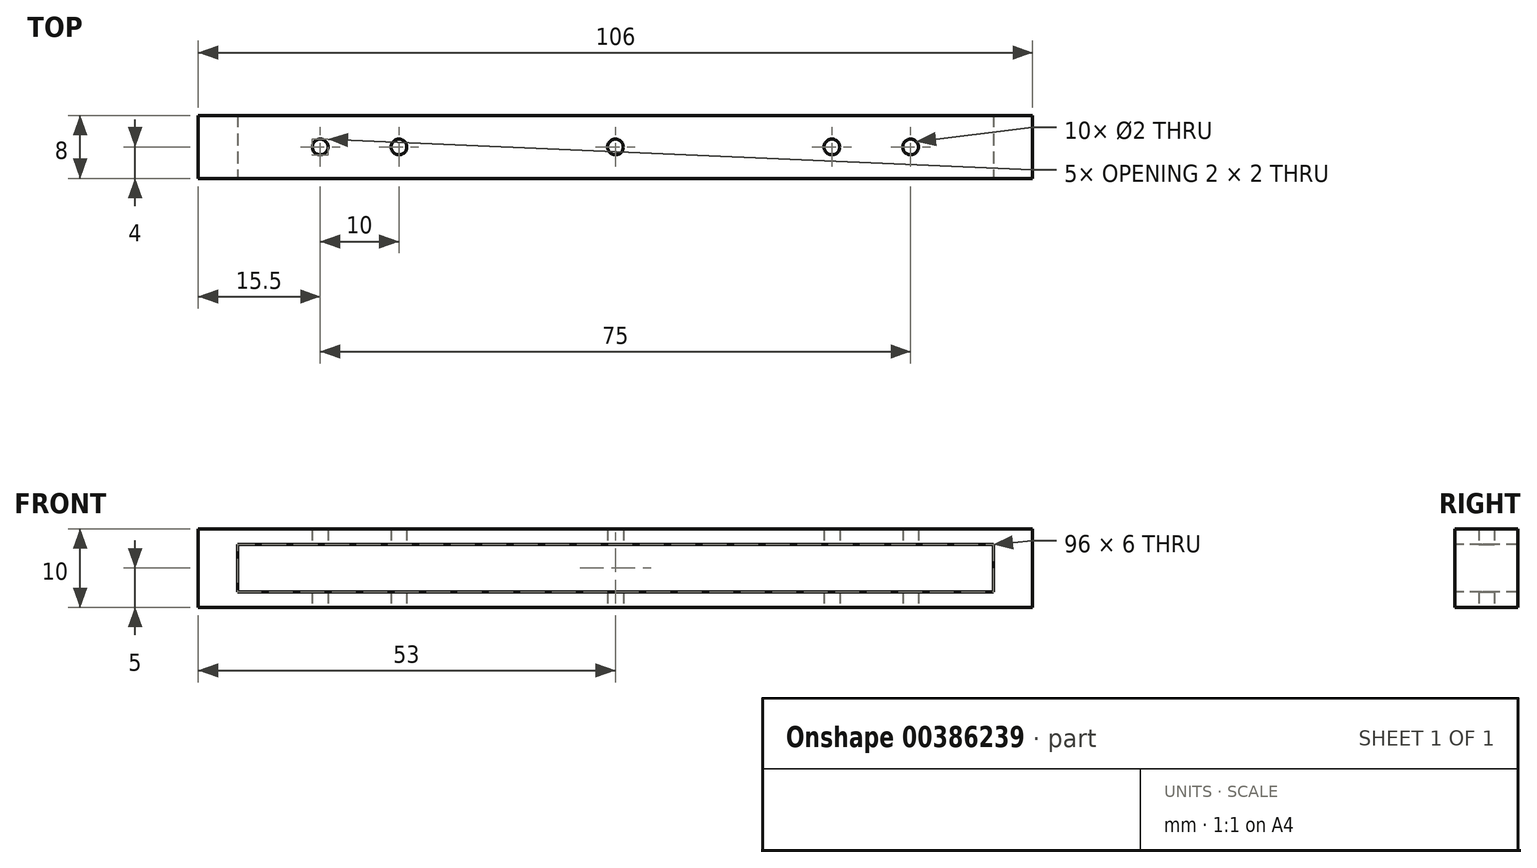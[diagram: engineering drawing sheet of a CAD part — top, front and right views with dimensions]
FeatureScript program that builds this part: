
annotation { "Feature Type Name" : "Feature", "Feature Type Description" : "" }
export const myFeature = defineFeature(function(context is Context, id is Id, definition is map)
    precondition{}
    {
        {
            assignVariable(context, id + "F0", {"name" : "height", "anyValue" : 10});
        }
        {
            var Q0;
            Q0=qCreatedBy(makeId("Top.planeOp"),FACE);
            var sketch = newSketch(context, id + "F1", { "sketchPlane" : qUnion([Q0])});
            skCircle(sketch, "E0", {"center": v(0, 0) * mm, "radius": 1 * mm});
            skCircle(sketch, "E1", {"center": v(37.5, 0) * mm, "radius": 1 * mm});
            skCircle(sketch, "E2", {"center": v(-37.5, 0) * mm, "radius": 1 * mm});
            skCircle(sketch, "E3", {"center": v(-27.5, 0) * mm, "radius": 1 * mm});
            skCircle(sketch, "E4", {"center": v(27.5, 0) * mm, "radius": 1 * mm});
            skLineSegment(sketch, "E5.bottom", {"start": v(-53, 4) * mm, "end": v(53, 4) * mm});
            skLineSegment(sketch, "E5.top", {"start": v(-53, -4) * mm, "end": v(53, -4) * mm});
            skLineSegment(sketch, "E5.left", {"start": v(-53, 4) * mm, "end": v(-53, -4) * mm});
            skLineSegment(sketch, "E5.right", {"start": v(53, 4) * mm, "end": v(53, -4) * mm});
            skSolve(sketch);
        }
        {
            var Q0;
            Q0=makeQuery(id+"F1.imprint","IMPRINT",FACE,{"disambiguationData":[TD([[makeQuery(id+"F1.imprint","IMPRINT",EDGE,{"derivedFrom":sQuery(id+"F1.wireOp",EDGE,"E0")}),-1.0]])]});
            var Q1;
            {var subQ0=sQuery(id+"F1.wireOp",EDGE,"E5.left");Q1=makeQuery(id+"F1.imprint","IMPRINT",FACE,{"disambiguationData":[TD([[makeQuery(id+"F1.imprint","IMPRINT",EDGE,{"derivedFrom":subQ0}),1.0]])]});}
            var Q2;
            {var subQ0=sQuery(id+"F1.wireOp",EDGE,"E5.right");Q2=makeQuery(id+"F1.imprint","IMPRINT",FACE,{"disambiguationData":[TD([[makeQuery(id+"F1.imprint","IMPRINT",EDGE,{"derivedFrom":subQ0}),-1.0]])]});}
            extrude(context, id + "F2", {"entities" : qUnion([Q0, Q1, Q2]), "depth" : (getVariable(context, 'height')) * mm});
        }
        {
            var Q0;
            Q0=makeQuery(id+"F2.opExtrude","SWEPT_FACE",FACE,{"disambiguationData":[OSD([sQuery(id+"F1.wireOp",EDGE,"E5.top")])]});
            var sketch = newSketch(context, id + "F3", { "sketchPlane" : qUnion([Q0])});
            skLineSegment(sketch, "E6.bottom", {"start": v(-48, 2) * mm, "end": v(48, 2) * mm});
            skLineSegment(sketch, "E6.top", {"start": v(-48, 8) * mm, "end": v(48, 8) * mm});
            skLineSegment(sketch, "E6.left", {"start": v(-48, 2) * mm, "end": v(-48, 8) * mm});
            skLineSegment(sketch, "E6.right", {"start": v(48, 2) * mm, "end": v(48, 8) * mm});
            skSolve(sketch);
        }
        {
            var Q0;
            Q0=makeQuery(id+"F3.imprint","IMPRINT",FACE,{"disambiguationData":[TD([[makeQuery(id+"F3.imprint","IMPRINT",EDGE,{"derivedFrom":sQuery(id+"F3.wireOp",EDGE,"E6.bottom")}),1.0]])]});
            extrude(context, id + "F4", {"entities" : qUnion([Q0]), "operationType" : NewBodyOperationType.REMOVE, "oppositeDirection" : true, "depth" : 25 * mm});
        }
    });
